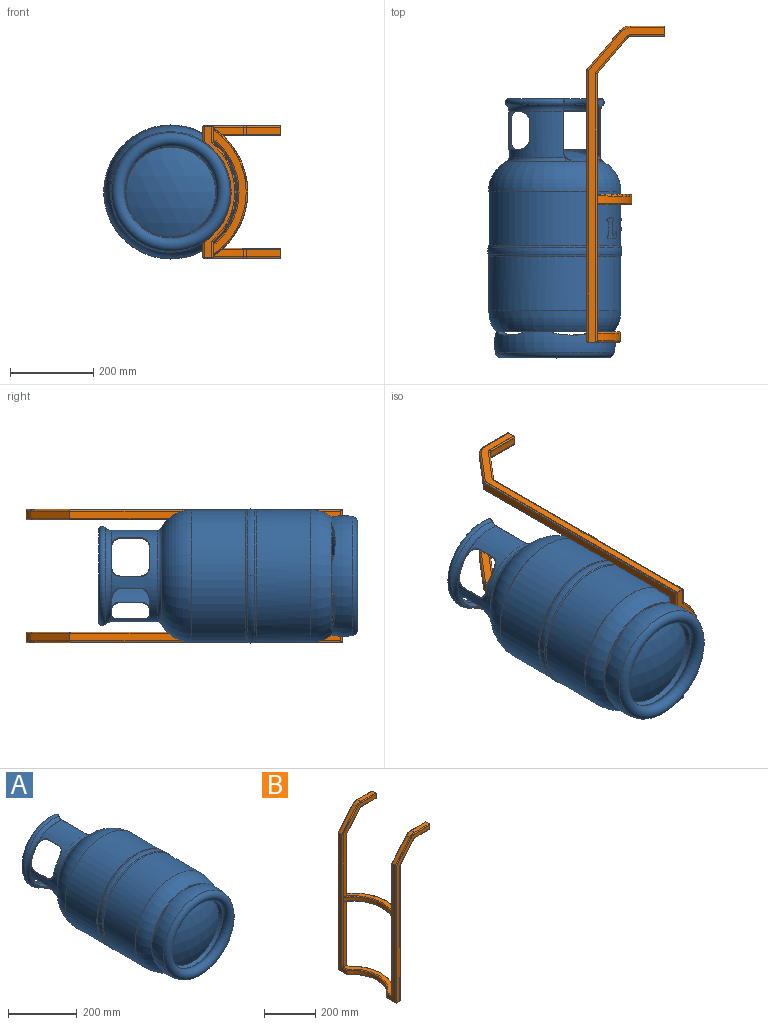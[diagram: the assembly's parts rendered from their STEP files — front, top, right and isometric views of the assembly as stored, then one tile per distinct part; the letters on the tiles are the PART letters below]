
ASSEMBLY  parts=2 mates=1
PART A: 195 faces, bbox 351.1x622.8x351.1 mm
  f0: torus R=127mm, axis (0,1,0), area 52168.6mm2, adj f16,f17
  f1: revolved ~322x161mm, area 9232mm2, adj f5,f6,f36
  f2: torus R=5mm, axis (0,-1,0), area 490.4mm2, adj f28,f32
  f3: torus R=110mm, axis (0,-1,0), area 22575.2mm2, adj f12,f13,f48,f52
  f4: cylinder r=159.1mm len=50mm, axis (0,-1,0), area 1436.8mm2, adj f128,f129,f130,f131,f132,f133,f134,f135
  f5: torus R=170mm, axis (0,-1,0), area 4380.5mm2, adj f1,f33,f36
  f6: torus R=170mm, axis (0,1,0), area 4380.5mm2, adj f1,f14,f36
  f7: torus R=121mm, axis (0,-1,0), area 6604.4mm2, adj f21,f32,f94,f95
  f8: cylinder r=1mm len=50mm, axis (0,-1,0), area 157.1mm2, adj f21,f22,f80,f81,f83,f86
  f9: cylinder r=1mm len=50mm, axis (0,-1,0), area 157.1mm2, adj f21,f22,f76,f77,f78,f79
  f10: cylinder r=1mm len=98.49mm, axis (0,-1,0), area 306.1mm2, adj f21,f22,f34,f53,f54,f55,f56
  f11: cylinder r=1mm len=98.49mm, axis (0,-1,0), area 306.1mm2, adj f21,f22,f35,f47,f49,f50,f51
  f12: torus R=130mm, axis (0,-1,0), area 8872.9mm2, adj f3,f21,f49,f54
  f13: torus R=88mm, axis (0,-1,0), area 7374.9mm2, adj f3,f22,f47,f53
  f14: cylinder r=159mm len=318mm, axis (0,-1,0), area 130299.4mm2, adj f6,f15
  f15: torus R=79mm, axis (0,-1,0), area 52435.7mm2, adj f14,f16,f38,f40,f42,f44,f46
  f16: torus R=46.35mm, axis (0,1,0), area 42883.7mm2, adj f0,f15,f37,f39,f41,f43,f45
  f17: torus R=46.35mm, axis (0,1,0), area 597.3mm2, adj f0,f18
  f18: torus R=79mm, axis (0,1,0), area 7285.3mm2, adj f17,f19
  f19: cone r=103.61mm half-angle=28.8deg, axis (0,-1,0), area 8167.4mm2, adj f18,f20
  f20: sphere r=244mm, area 39150.4mm2, adj f19
  f21: cylinder r=110mm len=220mm, axis (0,-1,0), area 31277mm2, adj f7,f8,f9,f10,f11,f12,f51,f56
  f22: cylinder r=108mm len=216mm, axis (0,-1,0), area 25755.8mm2, adj f8,f9,f10,f11,f13,f50,f55,f57
  f23: sphere r=242mm, area 38457.1mm2, adj f26
  f24: torus R=46.35mm, axis (0,1,0), area 8348mm2, adj f25,f31
  f25: torus R=79mm, axis (0,1,0), area 28085.8mm2, adj f24,f26,f37,f38,f39,f40,f41,f42
  f26: cone r=103.61mm half-angle=28.8deg, axis (0,-1,0), area 5650.5mm2, adj f23,f25
  f27: torus R=79mm, axis (0,-1,0), area 77657.1mm2, adj f32,f33
  f28: sphere r=242mm, area 45315.8mm2, adj f2,f29
  f29: torus R=79mm, axis (0,-1,0), area 74856.7mm2, adj f28,f30
  f30: cylinder r=157mm len=314mm, axis (0,-1,0), area 283545.1mm2, adj f29,f31
  f31: torus R=79mm, axis (0,-1,0), area 49322.8mm2, adj f24,f30
  f32: sphere r=244mm, area 32421.8mm2, adj f2,f7,f27,f91,f92,f93,f94,f95
  f33: cylinder r=159mm len=318mm, axis (0,-1,0), area 125889.8mm2, adj f5,f27,f96,f97,f98,f99,f100,f101
  f34: plane 29.04x15.75mm, normal (0.98,0,-0.19), area 234.1mm2, adj f10,f52,f53,f54
  f35: plane 29.04x16.04mm, normal (0,0,1), area 234.1mm2, adj f11,f47,f48,f49
  f36: revolved ~322x161mm, area 9232mm2, adj f1,f5,f6
  f37: bspline ~100x28.4mm, area 2391.9mm2, adj f16,f25,f38
  f38: plane 100x23.77mm, normal (0,-1,0), area 1389.2mm2, adj f15,f25,f37
  f39: bspline ~103.88x57.91mm, area 2394.9mm2, adj f16,f25,f40
  f40: plane 99.62x44.96mm, normal (0,-1,0), area 1389.2mm2, adj f15,f25,f39
  f41: bspline ~97.6x81.76mm, area 2394.9mm2, adj f16,f25,f42
  f42: plane 89.49x70.6mm, normal (0,-1,0), area 1389.2mm2, adj f15,f25,f41
  f43: bspline ~97.6x81.76mm, area 2394.9mm2, adj f16,f25,f44
  f44: plane 89.49x70.6mm, normal (0,-1,0), area 1389.2mm2, adj f15,f25,f43
  f45: bspline ~103.88x57.91mm, area 2394.9mm2, adj f16,f25,f46
  f46: plane 99.62x44.96mm, normal (0,-1,0), area 1389.2mm2, adj f15,f25,f45
  f47: bspline ~13.68x5.83mm, area 22.6mm2, adj f11,f13,f35,f48
  f48: bspline ~18.02x15.52mm, area 63.2mm2, adj f3,f35,f47,f49
  f49: bspline ~15.21x7.21mm, area 26mm2, adj f11,f12,f35,f48
  f50: bspline ~22.43x19.48mm, area 21.4mm2, adj f11,f22,f51,f91
  f51: bspline ~22.44x19.78mm, area 32mm2, adj f11,f21,f50,f94
  f52: bspline ~17.67x15.52mm, area 63.2mm2, adj f3,f34,f53,f54
  f53: bspline ~13.68x5.72mm, area 22.6mm2, adj f10,f13,f34,f52
  f54: bspline ~15.21x7.27mm, area 26mm2, adj f10,f12,f34,f52
  f55: bspline ~22.44x19.27mm, area 21.4mm2, adj f10,f22,f56,f93
  f56: bspline ~22.44x19.11mm, area 32mm2, adj f10,f21,f55,f95
  f57: bspline ~24.1x21mm, area 42.1mm2, adj f22,f58,f59,f60
  f58: cylinder r=1mm len=50mm, axis (0,-1,0), area 157.1mm2, adj f21,f22,f57,f59,f61,f64
  f59: bspline ~24.32x21.84mm, area 84.6mm2, adj f21,f57,f58,f60
  f60: torus R=109mm, axis (0,1,0), area 175.6mm2, adj f21,f22,f57,f59,f62,f65
  f61: bspline ~24.1x21mm, area 42.1mm2, adj f22,f58,f63,f64
  f62: bspline ~21x20.99mm, area 50.9mm2, adj f22,f60,f65,f66
  f63: torus R=109mm, axis (0,-1,0), area 175.6mm2, adj f21,f22,f61,f64,f67,f68
  f64: bspline ~24.32x21.84mm, area 84.6mm2, adj f21,f58,f61,f63
  f65: bspline ~21.19x21mm, area 49.9mm2, adj f21,f60,f62,f66
  f66: cylinder r=1mm len=50mm, axis (0,-1,0), area 157.1mm2, adj f21,f22,f62,f65,f67,f68
  f67: bspline ~21x20.99mm, area 50.9mm2, adj f22,f63,f66,f68
  f68: bspline ~21.19x21mm, area 49.9mm2, adj f21,f63,f66,f67
  f69: cylinder r=1mm len=50mm, axis (0,-1,0), area 157.1mm2, adj f21,f22,f70,f71,f72,f75
  f70: bspline ~21x19.7mm, area 50.9mm2, adj f22,f69,f72,f73
  f71: bspline ~21x19.7mm, area 50.9mm2, adj f22,f69,f74,f75
  f72: bspline ~21x19.58mm, area 49.9mm2, adj f21,f69,f70,f73
  f73: torus R=109mm, axis (0,-1,0), area 175.6mm2, adj f21,f22,f70,f72,f76,f78
  f74: torus R=109mm, axis (0,1,0), area 175.6mm2, adj f21,f22,f71,f75,f77,f79
  f75: bspline ~21x19.58mm, area 49.9mm2, adj f21,f69,f71,f74
  f76: bspline ~29.15x21mm, area 42.1mm2, adj f9,f22,f73,f78
  f77: bspline ~29.15x21mm, area 42.1mm2, adj f9,f22,f74,f79
  f78: bspline ~29.15x21mm, area 84.6mm2, adj f9,f21,f73,f76
  f79: bspline ~29.15x21mm, area 84.6mm2, adj f9,f21,f74,f77
  f80: bspline ~31.35x21mm, area 42.1mm2, adj f8,f22,f81,f82
  f81: bspline ~31.69x21mm, area 84.6mm2, adj f8,f21,f80,f82
  f82: torus R=109mm, axis (0,1,0), area 175.6mm2, adj f21,f22,f80,f81,f84,f87
  f83: bspline ~31.35x21mm, area 42.1mm2, adj f8,f22,f85,f86
  f84: bspline ~21x16.48mm, area 50.9mm2, adj f22,f82,f87,f88
  f85: torus R=109mm, axis (0,-1,0), area 175.6mm2, adj f21,f22,f83,f86,f89,f90
  f86: bspline ~31.69x21mm, area 84.6mm2, adj f8,f21,f83,f85
  f87: bspline ~21x16.05mm, area 49.9mm2, adj f21,f82,f84,f88
  f88: cylinder r=1mm len=50mm, axis (0,-1,0), area 157.1mm2, adj f21,f22,f84,f87,f89,f90
  f89: bspline ~21x16.48mm, area 50.9mm2, adj f22,f85,f88,f90
  f90: bspline ~21x16.05mm, area 49.9mm2, adj f21,f85,f88,f89
  f91: bspline ~20.46x17.75mm, area 230mm2, adj f32,f50,f92
  f92: torus R=97mm, axis (0,-1,0), area 10781.8mm2, adj f22,f32,f91,f93
  f93: bspline ~21.62x17.75mm, area 136.8mm2, adj f32,f55,f92
  f94: bspline ~14.32x9.77mm, area 60.1mm2, adj f7,f32,f51
  f95: bspline ~13.67x10.52mm, area 60.1mm2, adj f7,f32,f56
  f96: bspline ~2.35x1.08mm, area 0.3mm2, adj f33,f97,f126,f127
  f97: bspline ~2.75x1.31mm, area 0.3mm2, adj f33,f96,f98,f127
  f98: bspline ~1.42x0.73mm, area 0.2mm2, adj f33,f97,f99,f127
  f99: bspline ~3.44x2.37mm, area 0.5mm2, adj f33,f98,f100,f127
  f100: bspline ~8.32x2.63mm, area 0.9mm2, adj f33,f99,f101,f127
  f101: bspline ~6.88x4.97mm, area 1mm2, adj f33,f100,f102,f127
  f102: bspline ~3.65x1.77mm, area 0.4mm2, adj f33,f101,f103,f127
  f103: bspline ~3.28x2.69mm, area 0.4mm2, adj f33,f102,f104,f127
  f104: bspline ~8.24x4.71mm, area 1mm2, adj f33,f103,f105,f127
  f105: bspline ~12.23x9.41mm, area 1.8mm2, adj f33,f104,f106,f127
  f106: bspline ~14.19x4.13mm, area 1.5mm2, adj f33,f105,f107,f127
  f107: bspline ~7.92x4.67mm, area 1mm2, adj f33,f106,f108,f127
  f108: bspline ~4.53x3.93mm, area 0.7mm2, adj f33,f107,f109,f127
  f109: bspline ~2.5x0.95mm, area 0.3mm2, adj f33,f108,f110,f127
  f110: bspline ~2.6x1.11mm, area 0.3mm2, adj f33,f109,f111,f127
  f111: bspline ~3.37x3.34mm, area 0.5mm2, adj f33,f110,f112,f127
  f112: bspline ~4.1x3.67mm, area 0.6mm2, adj f33,f111,f113,f127
  f113: bspline ~9.09x3.95mm, area 1mm2, adj f33,f112,f114,f127
  f114: bspline ~8.99x4.58mm, area 1mm2, adj f33,f113,f115,f127
  f115: bspline ~4.29x3.41mm, area 0.6mm2, adj f33,f114,f116,f127
  f116: bspline ~3.27x2.84mm, area 0.5mm2, adj f33,f115,f117,f127
  f117: bspline ~2.41x2.15mm, area 0.4mm2, adj f33,f116,f118,f127
  f118: bspline ~9.58x5.38mm, area 1.1mm2, adj f33,f117,f119,f127
  f119: bspline ~15.22x6.45mm, area 1.8mm2, adj f33,f118,f120,f127
  f120: bspline ~13.69x4.32mm, area 1.5mm2, adj f33,f119,f121,f127
  f121: bspline ~10.14x9.95mm, area 1.5mm2, adj f33,f120,f122,f127
  f122: bspline ~11.73x2.89mm, area 1.2mm2, adj f33,f121,f123,f127
  f123: bspline ~12.11x3.42mm, area 1.3mm2, adj f33,f122,f124,f127
  f124: bspline ~10.05x9.51mm, area 1.4mm2, adj f33,f123,f125,f127
  f125: bspline ~12.6x3.99mm, area 1.4mm2, adj f33,f124,f126,f127
  f126: bspline ~8.18x3.25mm, area 0.9mm2, adj f33,f96,f125,f127
  f127: cylinder r=159.1mm len=51.88mm, axis (0,-1,0), area 1597mm2, adj f96,f97,f98,f99,f100,f101,f102,f103
  f128: bspline ~6.26x3.31mm, area 0.8mm2, adj f4,f33,f129,f150
  f129: bspline ~3.3x3.23mm, area 0.5mm2, adj f4,f33,f128,f130
  f130: bspline ~5.14x3.35mm, area 0.7mm2, adj f4,f33,f129,f131
  f131: bspline ~4.16x1.02mm, area 0.4mm2, adj f4,f33,f130,f132
  f132: plane 2.12x0.52mm, normal (0,1,0), area 0.2mm2, adj f4,f33,f131,f133
  f133: bspline ~14.05x2.18mm, area 1.4mm2, adj f4,f33,f132,f134
  f134: bspline ~3.76x0.44mm, area 0.4mm2, adj f4,f33,f133,f135
  f135: bspline ~10.4x2.38mm, area 1.1mm2, adj f4,f33,f134,f136
  f136: bspline ~13.04x7.95mm, area 1.6mm2, adj f4,f33,f135,f137
  f137: bspline ~11.59x5.41mm, area 1.3mm2, adj f4,f33,f136,f138
  f138: bspline ~12.32x4.08mm, area 1.3mm2, adj f4,f33,f137,f139
  f139: bspline ~4.5x0.5mm, area 0.5mm2, adj f4,f33,f138,f140
  f140: bspline ~1.76x0.29mm, area 0.2mm2, adj f4,f33,f139,f141
  f141: bspline ~1.18x1.01mm, area 0.2mm2, adj f4,f33,f140,f142
  f142: plane 0.22x0.1mm, normal (0.12,0,-0.99), area 0mm2, adj f4,f33,f141,f143
  f143: plane 5.97x0.22mm, normal (0.12,0.04,-0.99), area 0.6mm2, adj f4,f33,f142,f144
  f144: bspline ~4.37x2.51mm, area 0.5mm2, adj f4,f33,f143,f145
  f145: bspline ~2.77x2.01mm, area 0.4mm2, adj f4,f33,f144,f146
  f146: bspline ~12.71x4.76mm, area 1.5mm2, adj f4,f33,f145,f147
  f147: bspline ~12.6x4.57mm, area 1.5mm2, adj f4,f33,f146,f148
  f148: bspline ~3.3x2.99mm, area 0.5mm2, adj f4,f33,f147,f149
  f149: bspline ~9.79x1.66mm, area 1mm2, adj f4,f33,f148,f150
  f150: plane 18.93x0.1mm, normal (-0.22,0,0.98), area 1.9mm2, adj f4,f33,f128,f149
  f151: bspline ~1.58x0.61mm, area 0.2mm2, adj f4,f152,f158,f159
  f152: bspline ~2.59x0.48mm, area 0.3mm2, adj f4,f151,f153,f159
  f153: bspline ~3.94x1.25mm, area 0.4mm2, adj f4,f152,f154,f159
  f154: bspline ~6.02x2.31mm, area 0.7mm2, adj f4,f153,f155,f159
  f155: bspline ~6.36x2.7mm, area 0.7mm2, adj f4,f154,f156,f159
  f156: bspline ~4.12x1.25mm, area 0.4mm2, adj f4,f155,f157,f159
  f157: bspline ~2.62x1.32mm, area 0.3mm2, adj f4,f156,f158,f159
  f158: plane 11.49x0.1mm, normal (0.12,0,-0.99), area 1.1mm2, adj f4,f151,f157,f159
  f159: cylinder r=159mm len=14.87mm, axis (0,-1,0), area 114.7mm2, adj f151,f152,f153,f154,f155,f156,f157,f158
  f160: bspline ~7.05x0.85mm, area 0.7mm2, adj f33,f161,f185,f186
  f161: bspline ~4.2x2.33mm, area 0.5mm2, adj f33,f160,f162,f186
  f162: bspline ~8.35x7.19mm, area 1.3mm2, adj f33,f161,f163,f186
  f163: bspline ~2.27x2.27mm, area 0.4mm2, adj f33,f162,f164,f186
  f164: bspline ~6.07x4.03mm, area 0.8mm2, adj f33,f163,f165,f186
  f165: bspline ~9.41x3.07mm, area 1mm2, adj f33,f164,f166,f186
  f166: bspline ~3.43x2.77mm, area 0.5mm2, adj f33,f165,f167,f186
  f167: plane 7.15x3.51mm, normal (-0.04,-1,0.08), area 0.8mm2, adj f33,f166,f168,f186
  f168: plane 21.2x13.09mm, normal (0,-1,0), area 2.5mm2, adj f33,f167,f169,f186
  f169: bspline ~2.82x2.14mm, area 0.4mm2, adj f33,f168,f170,f186
  f170: bspline ~2.46x1.22mm, area 0.3mm2, adj f33,f169,f171,f186
  f171: bspline ~2.85x2.38mm, area 0.4mm2, adj f33,f170,f172,f186
  f172: bspline ~2.7x2.23mm, area 0.4mm2, adj f33,f171,f173,f186
  f173: bspline ~8.51x0.44mm, area 0.8mm2, adj f33,f172,f174,f186
  f174: bspline ~9.44x0.21mm, area 1mm2, adj f33,f173,f175,f186
  f175: bspline ~8.9x0.23mm, area 0.9mm2, adj f33,f174,f176,f186
  f176: bspline ~5.42x1.9mm, area 0.6mm2, adj f33,f175,f177,f186
  f177: bspline ~2.42x1.87mm, area 0.3mm2, adj f33,f176,f178,f186
  f178: bspline ~2.03x0.95mm, area 0.2mm2, adj f33,f177,f179,f186
  f179: bspline ~3.96x3.43mm, area 0.6mm2, adj f33,f178,f180,f186
  f180: bspline ~7.99x5.6mm, area 1mm2, adj f33,f179,f181,f186
  f181: bspline ~8.73x5.35mm, area 1mm2, adj f33,f180,f182,f186
  f182: bspline ~3.86x3.8mm, area 0.6mm2, adj f33,f181,f183,f186
  f183: bspline ~3.25x2.65mm, area 0.5mm2, adj f33,f182,f184,f186
  f184: bspline ~8.35x1.6mm, area 0.9mm2, adj f33,f183,f185,f186
  f185: plane 16.18x0.09mm, normal (0.49,0,-0.87), area 1.6mm2, adj f33,f160,f184,f186
  f186: cylinder r=159.1mm len=50mm, axis (0,-1,0), area 1167.1mm2, adj f160,f161,f162,f163,f164,f165,f166,f167
  f187: torus R=127mm, axis (0,1,0), area 21531.5mm2, adj f189,f194
  f188: torus R=79mm, axis (0,-1,0), area 15035.3mm2, adj f193,f194
  f189: torus R=127.77mm, axis (0,1,0), area 6349.9mm2, adj f187,f190
  f190: torus R=46.35mm, axis (0,1,0), area 12505.7mm2, adj f189,f191
  f191: torus R=127.88mm, axis (0,1,0), area 8510.9mm2, adj f190,f192
  f192: torus R=79mm, axis (0,1,0), area 5901mm2, adj f191,f193
  f193: cone r=117.54mm half-angle=28.8deg, axis (0,-1,0), area 1483.1mm2, adj f188,f192
  f194: torus R=46.35mm, axis (0,1,0), area 33508.6mm2, adj f187,f188
PART B: 210 faces, bbox 187.9x335.9x763.7 mm
  f0: plane 642.74x37.8mm, normal (-1,0,0), area 10836mm2, adj f1,f2,f9,f19,f162,f170,f175,f182
  f1: cylinder r=2.02mm len=309mm, axis (0,0,-1), area 965mm2, adj f0,f3,f175,f186
  f2: cylinder r=2.02mm len=291.43mm, axis (0,0,-1), area 912mm2, adj f0,f3,f20,f185
  f3: plane 733.02x182.8mm, normal (0,-1,0), area 13983.8mm2, adj f1,f2,f10,f20,f21,f32,f33,f44
  f4: plane 731.97x183.75mm, normal (0,1,0), area 14021.9mm2, adj f5,f6,f17,f24,f29,f36,f41,f48
  f5: cylinder r=4mm len=309mm, axis (0,0,-1), area 1928.9mm2, adj f4,f7,f74,f166
  f6: cylinder r=4mm len=291.43mm, axis (0,0,-1), area 1826.5mm2, adj f4,f7,f24,f78
  f7: plane 642.03x36.86mm, normal (1,0,0), area 10839.6mm2, adj f5,f6,f13,f25,f74,f78,f79,f80
  f8: plane 753.4x182.18mm, normal (0,1,0), area 14694mm2, adj f9,f12,f18,f23,f30,f35,f42,f47
  f9: cylinder r=2.02mm len=644.43mm, axis (0,0,-1), area 2014.9mm2, adj f0,f8,f18,f170
  f10: cylinder r=2.02mm len=632.42mm, axis (0,0,-1), area 1977.2mm2, adj f3,f11,f21,f173
  f11: plane 649.42x46.98mm, normal (1,0,0), area 11549.8mm2, adj f10,f12,f22,f172,f173,f176
  f12: cylinder r=2.02mm len=651.42mm, axis (0,0,-1), area 2036.8mm2, adj f8,f11,f23,f172
  f13: cylinder r=4mm len=646.43mm, axis (0,0,-1), area 4044.4mm2, adj f7,f14,f26,f165
  f14: plane 755.23x182mm, normal (0,-1,0), area 14736mm2, adj f13,f15,f26,f27,f38,f39,f48,f51
  f15: cylinder r=4mm len=654.15mm, axis (0,0,-1), area 4092.9mm2, adj f14,f16,f27,f163
  f16: plane 650.15x47.96mm, normal (-1,0,0), area 11578.9mm2, adj f15,f17,f28,f154,f163,f168
  f17: cylinder r=4mm len=633.15mm, axis (0,0,-1), area 3961mm2, adj f4,f16,f29,f168
  f18: cylinder r=2.02mm len=89.04mm, axis (-0.65,0,-0.76), area 359.6mm2, adj f8,f9,f19,f30
  f19: plane 87.18x74.1mm, normal (-0.76,0,0.65), area 1945.1mm2, adj f0,f18,f20,f31
  f20: cylinder r=2.02mm len=89.04mm, axis (-0.65,0,-0.76), area 359.6mm2, adj f2,f3,f19,f32
  f21: cylinder r=2.02mm len=94.36mm, axis (-0.65,0,-0.76), area 381.5mm2, adj f3,f10,f22,f33
  f22: plane 93.06x79.1mm, normal (0.76,0,-0.65), area 2076.3mm2, adj f11,f21,f23,f34
  f23: cylinder r=2.02mm len=94.36mm, axis (-0.65,0,-0.76), area 381.5mm2, adj f8,f12,f22,f35
  f24: cylinder r=4mm len=90.33mm, axis (-0.65,0,-0.76), area 718.9mm2, adj f4,f6,f25,f36
  f25: plane 86.62x73.62mm, normal (0.76,0,-0.65), area 1932.6mm2, adj f7,f24,f26,f37
  f26: cylinder r=4mm len=90.33mm, axis (-0.65,0,-0.76), area 718.9mm2, adj f13,f14,f25,f38
  f27: cylinder r=4mm len=96.21mm, axis (-0.65,0,-0.76), area 767.4mm2, adj f14,f15,f28,f39
  f28: plane 93.62x79.58mm, normal (-0.76,0,0.65), area 2088.8mm2, adj f16,f27,f29,f40
  f29: cylinder r=4mm len=96.21mm, axis (-0.65,0,-0.76), area 767.4mm2, adj f4,f17,f28,f41
  f30: torus R=11.52mm, axis (0,-1,0), area 27.8mm2, adj f8,f18,f31,f42
  f31: cylinder r=9.5mm len=17mm, axis (0,-1,0), area 139.9mm2, adj f19,f30,f32,f43
  f32: torus R=11.52mm, axis (0,-1,0), area 27.8mm2, adj f3,f20,f31,f44
  f33: torus R=28.48mm, axis (0,-1,0), area 80.8mm2, adj f3,f21,f34,f45
  f34: cylinder r=30.5mm len=23.24mm, axis (0,-1,0), area 449.2mm2, adj f22,f33,f35,f46
  f35: torus R=28.48mm, axis (0,-1,0), area 80.8mm2, adj f8,f23,f34,f47
  f36: torus R=11.5mm, axis (0,-1,0), area 48.7mm2, adj f4,f24,f37,f49
  f37: cylinder r=7.5mm len=17mm, axis (0,-1,0), area 110.5mm2, adj f25,f36,f38,f50
  f38: torus R=11.5mm, axis (0,-1,0), area 48.7mm2, adj f14,f26,f37,f51
  f39: torus R=28.5mm, axis (0,-1,0), area 169mm2, adj f14,f27,f40,f52
  f40: cylinder r=32.5mm len=24.76mm, axis (0,-1,0), area 478.6mm2, adj f28,f39,f41,f53
  f41: torus R=28.5mm, axis (0,-1,0), area 169mm2, adj f4,f29,f40,f54
  f42: cylinder r=2.02mm len=81.66mm, axis (-1,0,0), area 255.9mm2, adj f8,f30,f43,f48
  f43: plane 81.66x17mm, normal (0,0,1), area 1388.3mm2, adj f31,f42,f44,f48
  f44: cylinder r=2.02mm len=81.66mm, axis (-1,0,0), area 255.9mm2, adj f3,f32,f43,f48
  f45: cylinder r=2.02mm len=81.66mm, axis (-1,0,0), area 255.9mm2, adj f3,f33,f46,f48
  f46: plane 81.66x17mm, normal (0,0,-1), area 1388.3mm2, adj f34,f45,f47,f48
  f47: cylinder r=2.02mm len=81.66mm, axis (-1,0,0), area 255.9mm2, adj f8,f35,f46,f48
  f48: plane 25x25mm, normal (1,0,0), area 173.8mm2, adj f3,f4,f8,f14,f42,f43,f44,f45
  f49: cylinder r=4mm len=81.66mm, axis (-1,0,0), area 513.1mm2, adj f4,f36,f48,f50
  f50: plane 81.66x17mm, normal (0,0,-1), area 1388.3mm2, adj f37,f48,f49,f51
  f51: cylinder r=4mm len=81.66mm, axis (-1,0,0), area 513.1mm2, adj f14,f38,f48,f50
  f52: cylinder r=4mm len=81.66mm, axis (-1,0,0), area 513.1mm2, adj f14,f39,f48,f53
  f53: plane 81.66x17mm, normal (0,0,1), area 1388.3mm2, adj f40,f48,f52,f54
  f54: cylinder r=4mm len=81.66mm, axis (-1,0,0), area 513.1mm2, adj f4,f41,f48,f53
  f55: plane 21.9x12.38mm, normal (0,1,0), area 237.9mm2, adj f57,f67,f68,f71,f72,f73
  f56: plane 21.51x14.81mm, normal (-1,0,0), area 298.2mm2, adj f57,f64,f65,f66,f67,f68
  f57: cylinder r=2.02mm len=21mm, axis (0,0,1), area 65.8mm2, adj f55,f56,f67,f68
  f58: plane 25x21mm, normal (-0.86,0.52,0), area 165.5mm2, adj f59,f61,f62,f63,f64,f65,f66,f67
  f59: torus R=181mm, axis (0,0,1), area 37.5mm2, adj f58,f60,f63,f132,f142
  f60: cylinder r=185mm len=17mm, axis (0,0,1), area 74.4mm2, adj f59,f61,f132,f142
  f61: torus R=181mm, axis (0,0,1), area 37.5mm2, adj f58,f60,f62,f132,f142
  f62: plane 17.77x14.91mm, normal (0,0,1), area 180mm2, adj f58,f61,f69,f125,f129,f142
  f63: plane 17.77x14.91mm, normal (0,0,-1), area 180mm2, adj f58,f59,f70,f129,f131,f142
  f64: torus R=180.98mm, axis (0,0,1), area 20.7mm2, adj f56,f58,f65,f68
  f65: cylinder r=183mm len=17mm, axis (0,0,1), area 101.5mm2, adj f56,f58,f64,f66
  f66: torus R=180.98mm, axis (0,0,1), area 20.7mm2, adj f56,f58,f65,f67
  f67: plane 17.77x14.91mm, normal (0,0,1), area 180mm2, adj f55,f56,f57,f58,f66,f71
  f68: plane 17.77x14.91mm, normal (0,0,-1), area 180mm2, adj f55,f56,f57,f58,f64,f73
  f69: torus R=164mm, axis (0,0,1), area 14.8mm2, adj f58,f62,f129
  f70: torus R=164mm, axis (0,0,1), area 14.8mm2, adj f58,f63,f129
  f71: torus R=164.02mm, axis (0,0,1), area 14mm2, adj f55,f58,f67,f72
  f72: cylinder r=162mm len=17mm, axis (0,0,1), area 49.2mm2, adj f55,f58,f71,f73
  f73: torus R=164.02mm, axis (0,0,1), area 14mm2, adj f55,f58,f68,f72
  f74: plane 299.12x87.88mm, normal (0,0,-1), area 5566.7mm2, adj f4,f5,f7,f75,f81,f121,f130,f138
  f75: torus R=164mm, axis (0,0,1), area 1999.5mm2, adj f4,f74,f76,f121
  f76: cylinder r=160mm len=270mm, axis (0,0,1), area 5463mm2, adj f4,f75,f77,f121
  f77: torus R=164mm, axis (0,0,1), area 1999.5mm2, adj f4,f76,f78,f121
  f78: plane 299.12x87.88mm, normal (0,0,1), area 5566.7mm2, adj f4,f6,f7,f77,f79,f120,f121,f138
  f79: torus R=181mm, axis (0,0,1), area 2260.1mm2, adj f7,f78,f80,f138
  f80: cylinder r=185mm len=308.76mm, axis (0,0,1), area 6209.4mm2, adj f7,f79,f81,f138
  f81: torus R=181mm, axis (0,0,1), area 2260.1mm2, adj f7,f74,f80,f138
  f82: cylinder r=4mm len=81.66mm, axis (1,0,0), area 513.1mm2, adj f83,f88,f95,f124
  f83: plane 81.66x17mm, normal (0,0,-1), area 1388.3mm2, adj f82,f84,f88,f96
  f84: cylinder r=4mm len=81.66mm, axis (1,0,0), area 513.1mm2, adj f83,f88,f97,f121
  f85: cylinder r=4mm len=81.66mm, axis (1,0,0), area 513.1mm2, adj f86,f88,f98,f121
  f86: plane 81.66x17mm, normal (0,0,1), area 1388.3mm2, adj f85,f87,f88,f99
  f87: cylinder r=4mm len=81.66mm, axis (1,0,0), area 513.1mm2, adj f86,f88,f100,f124
  f88: plane 25x25mm, normal (1,0,0), area 173.8mm2, adj f82,f83,f84,f85,f86,f87,f89,f90
  f89: cylinder r=2.02mm len=81.66mm, axis (1,0,0), area 255.9mm2, adj f88,f90,f101,f129
  f90: plane 81.66x17mm, normal (0,0,1), area 1388.3mm2, adj f88,f89,f91,f102
  f91: cylinder r=2.02mm len=81.66mm, axis (1,0,0), area 255.9mm2, adj f88,f90,f103,f132
  f92: cylinder r=2.02mm len=81.66mm, axis (1,0,0), area 255.9mm2, adj f88,f93,f104,f132
  f93: plane 81.66x17mm, normal (0,0,-1), area 1388.3mm2, adj f88,f92,f94,f105
  f94: cylinder r=2.02mm len=81.66mm, axis (1,0,0), area 255.9mm2, adj f88,f93,f106,f129
  f95: torus R=11.5mm, axis (0,1,0), area 48.7mm2, adj f82,f96,f107,f124
  f96: cylinder r=7.5mm len=17mm, axis (0,1,0), area 110.5mm2, adj f83,f95,f97,f108
  f97: torus R=11.5mm, axis (0,1,0), area 48.7mm2, adj f84,f96,f109,f121
  f98: torus R=28.5mm, axis (0,1,0), area 169mm2, adj f85,f99,f110,f121
  f99: cylinder r=32.5mm len=24.76mm, axis (0,1,0), area 478.6mm2, adj f86,f98,f100,f111
  f100: torus R=28.5mm, axis (0,1,0), area 169mm2, adj f87,f99,f112,f124
  f101: torus R=11.52mm, axis (0,1,0), area 27.8mm2, adj f89,f102,f113,f129
  f102: cylinder r=9.5mm len=17mm, axis (0,1,0), area 139.9mm2, adj f90,f101,f103,f114
  f103: torus R=11.52mm, axis (0,1,0), area 27.8mm2, adj f91,f102,f115,f132
  f104: torus R=28.48mm, axis (0,1,0), area 80.8mm2, adj f92,f105,f116,f132
  f105: cylinder r=30.5mm len=23.24mm, axis (0,1,0), area 449.2mm2, adj f93,f104,f106,f117
  f106: torus R=28.48mm, axis (0,1,0), area 80.8mm2, adj f94,f105,f118,f129
  f107: cylinder r=4mm len=90.33mm, axis (0.65,0,0.76), area 718.9mm2, adj f95,f108,f119,f124
  f108: plane 86.62x73.62mm, normal (0.76,0,-0.65), area 1932.6mm2, adj f96,f107,f109,f138
  f109: cylinder r=4mm len=90.33mm, axis (0.65,0,0.76), area 718.9mm2, adj f97,f108,f120,f121
  f110: cylinder r=4mm len=96.21mm, axis (0.65,0,0.76), area 767.4mm2, adj f98,f111,f121,f122
  f111: plane 93.62x79.58mm, normal (-0.76,0,0.65), area 2088.8mm2, adj f99,f110,f112,f135
  f112: cylinder r=4mm len=96.21mm, axis (0.65,0,0.76), area 767.4mm2, adj f100,f111,f123,f124
  f113: cylinder r=2.02mm len=89.04mm, axis (0.65,0,0.76), area 359.6mm2, adj f101,f114,f125,f129
  f114: plane 87.18x74.1mm, normal (-0.76,0,0.65), area 1945.1mm2, adj f102,f113,f115,f142
  f115: cylinder r=2.02mm len=89.04mm, axis (0.65,0,0.76), area 359.6mm2, adj f103,f114,f126,f132
  f116: cylinder r=2.02mm len=94.36mm, axis (0.65,0,0.76), area 381.5mm2, adj f104,f117,f127,f132
  f117: plane 93.06x79.1mm, normal (0.76,0,-0.65), area 2076.3mm2, adj f105,f116,f118,f145
  f118: cylinder r=2.02mm len=94.36mm, axis (0.65,0,0.76), area 381.5mm2, adj f106,f117,f128,f129
  f119: cylinder r=4mm len=646.43mm, axis (0,0,1), area 4044.4mm2, adj f107,f124,f137,f138
  f120: cylinder r=4mm len=291.43mm, axis (0,0,1), area 1826.5mm2, adj f78,f109,f121,f138
  f121: plane 731.97x183.75mm, normal (0,-1,0), area 14021.9mm2, adj f74,f75,f76,f77,f78,f84,f85,f88
  f122: cylinder r=4mm len=633.15mm, axis (0,0,1), area 3961mm2, adj f110,f121,f134,f135
  f123: cylinder r=4mm len=654.15mm, axis (0,0,1), area 4092.9mm2, adj f112,f124,f135,f136
  f124: plane 755.23x182mm, normal (0,1,0), area 14736mm2, adj f82,f87,f88,f95,f100,f107,f112,f119
  f125: cylinder r=2.02mm len=291.43mm, axis (0,0,1), area 912mm2, adj f62,f113,f129,f142
  f126: cylinder r=2.02mm len=644.43mm, axis (0,0,1), area 2014.9mm2, adj f115,f132,f142,f143
  f127: cylinder r=2.02mm len=651.42mm, axis (0,0,1), area 2036.8mm2, adj f116,f132,f144,f145
  f128: cylinder r=2.02mm len=632.42mm, axis (0,0,1), area 1977.2mm2, adj f118,f129,f140,f145
  f129: plane 733.02x182.8mm, normal (0,1,0), area 13983.8mm2, adj f58,f62,f63,f69,f70,f88,f89,f94
  f130: cylinder r=4mm len=309mm, axis (0,0,1), area 1928.9mm2, adj f74,f121,f133,f138
  f131: cylinder r=2.02mm len=309mm, axis (0,0,1), area 965mm2, adj f63,f129,f141,f142
  f132: plane 753.4x182.18mm, normal (0,-1,0), area 14694mm2, adj f58,f59,f60,f61,f88,f91,f92,f103
  f133: cylinder r=4mm len=20.74mm, axis (0,1,0), area 111.6mm2, adj f130,f138,f139,f167
  f134: cylinder r=4mm len=30.96mm, axis (0,1,0), area 174.1mm2, adj f122,f135,f153,f167
  f135: plane 650.15x47.96mm, normal (-1,0,0), area 11578.9mm2, adj f111,f122,f123,f134,f136,f153
  f136: cylinder r=4mm len=51.96mm, axis (0,1,0), area 312.9mm2, adj f123,f135,f153,f164
  f137: cylinder r=4mm len=41.74mm, axis (0,1,0), area 243.5mm2, adj f119,f138,f139,f164
  f138: plane 642.03x36.86mm, normal (1,0,0), area 10839.5mm2, adj f74,f78,f79,f80,f81,f108,f119,f120
  f139: plane 25.82x4.82mm, normal (0.44,-0.9,0), area 3.1mm2, adj f133,f137,f138,f148,f149,f150
  f140: cylinder r=2.02mm len=29.98mm, axis (0,1,0), area 89.3mm2, adj f128,f145,f146,f174
  f141: cylinder r=2.02mm len=20.74mm, axis (0,1,0), area 60.3mm2, adj f131,f142,f161,f174
  f142: plane 642.74x37.8mm, normal (-1,0,0), area 10836mm2, adj f59,f60,f61,f62,f63,f114,f125,f126
  f143: cylinder r=2.02mm len=39.74mm, axis (0,1,0), area 119.8mm2, adj f126,f142,f161,f171
  f144: cylinder r=2.02mm len=48.98mm, axis (0,1,0), area 148.8mm2, adj f127,f145,f146,f171
  f145: plane 649.42x46.98mm, normal (1,0,0), area 11549.8mm2, adj f117,f127,f128,f140,f144,f146
  f146: plane 21.41x2.51mm, normal (0.44,-0.9,0), area 2.3mm2, adj f140,f144,f145,f156,f157,f158,f171,f174
  f147: torus R=136.5mm, axis (0,0,1), area 1589.9mm2, adj f152,f153,f154,f164
  f148: torus R=153.5mm, axis (0,0,1), area 1709.7mm2, adj f139,f149,f164,f169
  f149: cylinder r=157.5mm len=240.31mm, axis (0,0,1), area 4647mm2, adj f139,f148,f150,f169
  f150: torus R=153.5mm, axis (0,0,1), area 1709.7mm2, adj f139,f149,f167,f169
  f151: torus R=136.5mm, axis (0,0,1), area 1589.9mm2, adj f152,f153,f154,f167
  f152: cylinder r=132.5mm len=215.95mm, axis (0,0,1), area 4291.2mm2, adj f147,f151,f153,f154
  f153: plane 25.82x4.9mm, normal (-0.44,0.9,0), area 3.8mm2, adj f134,f135,f136,f147,f151,f152
  f154: plane 25.82x4.9mm, normal (-0.44,-0.9,0), area 3.8mm2, adj f16,f147,f151,f152,f163,f168
  f155: torus R=153.48mm, axis (0,0,1), area 849.2mm2, adj f160,f161,f162,f171
  f156: torus R=136.52mm, axis (0,0,1), area 797mm2, adj f146,f157,f171,f176
  f157: cylinder r=134.5mm len=217.94mm, axis (0,0,1), area 4318.9mm2, adj f146,f156,f158,f176
  f158: torus R=136.52mm, axis (0,0,1), area 797mm2, adj f146,f157,f174,f176
  f159: torus R=153.48mm, axis (0,0,1), area 849.2mm2, adj f160,f161,f162,f174
  f160: cylinder r=155.5mm len=238.4mm, axis (0,0,1), area 4617.9mm2, adj f155,f159,f161,f162
  f161: plane 21.4x2.42mm, normal (-0.44,0.9,0), area 1.9mm2, adj f141,f142,f143,f155,f159,f160
  f162: plane 21.4x2.4mm, normal (-0.44,-0.9,0), area 1.9mm2, adj f0,f155,f159,f160,f170,f175
  f163: cylinder r=4mm len=51.96mm, axis (0,1,0), area 312.9mm2, adj f15,f16,f154,f164
  f164: plane 320x72.62mm, normal (0,0,-1), area 6026.9mm2, adj f14,f124,f136,f137,f147,f148,f163,f165
  f165: cylinder r=4mm len=41.74mm, axis (0,1,0), area 243.5mm2, adj f7,f13,f164,f169
  f166: cylinder r=4mm len=20.74mm, axis (0,1,0), area 111.6mm2, adj f5,f7,f167,f169
  f167: plane 270x72.62mm, normal (0,0,1), area 5176.9mm2, adj f4,f121,f133,f134,f150,f151,f166,f168
  f168: cylinder r=4mm len=30.96mm, axis (0,1,0), area 174.1mm2, adj f16,f17,f154,f167
  f169: plane 25.82x4.82mm, normal (0.44,0.9,0), area 3.1mm2, adj f7,f148,f149,f150,f165,f166
  f170: cylinder r=2.02mm len=39.74mm, axis (0,1,0), area 119.8mm2, adj f0,f9,f162,f171
  f171: plane 316x72.62mm, normal (0,0,1), area 5958.9mm2, adj f8,f132,f143,f144,f146,f155,f156,f170
  f172: cylinder r=2.02mm len=48.98mm, axis (0,1,0), area 148.8mm2, adj f11,f12,f171,f176
  f173: cylinder r=2.02mm len=29.98mm, axis (0,1,0), area 89.3mm2, adj f10,f11,f174,f176
  f174: plane 274x72.62mm, normal (0,0,-1), area 5244.9mm2, adj f3,f129,f140,f141,f146,f158,f159,f173
  f175: cylinder r=2.02mm len=20.74mm, axis (0,1,0), area 60.3mm2, adj f0,f1,f162,f174
  f176: plane 21.41x2.51mm, normal (0.44,0.9,0), area 2.3mm2, adj f11,f156,f157,f158,f171,f172,f173,f174
  f177: torus R=164mm, axis (0,0,1), area 14.8mm2, adj f3,f185,f192
  f178: torus R=164mm, axis (0,0,1), area 14.8mm2, adj f3,f186,f192
  f179: torus R=164.02mm, axis (0,0,1), area 14mm2, adj f180,f190,f192,f193
  f180: cylinder r=162mm len=17mm, axis (0,0,1), area 49.2mm2, adj f179,f181,f192,f193
  f181: torus R=164.02mm, axis (0,0,1), area 14mm2, adj f180,f191,f192,f193
  f182: torus R=181mm, axis (0,0,1), area 37.5mm2, adj f0,f8,f183,f186,f192
  f183: cylinder r=185mm len=17mm, axis (0,0,1), area 74.4mm2, adj f0,f8,f182,f184
  f184: torus R=181mm, axis (0,0,1), area 37.5mm2, adj f0,f8,f183,f185,f192
  f185: plane 17.77x14.91mm, normal (0,0,1), area 180mm2, adj f0,f2,f3,f177,f184,f192
  f186: plane 17.77x14.91mm, normal (0,0,-1), area 180mm2, adj f0,f1,f3,f178,f182,f192
  f187: torus R=180.98mm, axis (0,0,1), area 20.7mm2, adj f188,f191,f192,f195
  f188: cylinder r=183mm len=17mm, axis (0,0,1), area 101.5mm2, adj f187,f189,f192,f195
  f189: torus R=180.98mm, axis (0,0,1), area 20.7mm2, adj f188,f190,f192,f195
  f190: plane 17.77x14.91mm, normal (0,0,1), area 180mm2, adj f179,f189,f192,f193,f194,f195
  f191: plane 17.77x14.91mm, normal (0,0,-1), area 180mm2, adj f181,f187,f192,f193,f194,f195
  f192: plane 25x21mm, normal (-0.86,-0.52,0), area 165.5mm2, adj f3,f8,f177,f178,f179,f180,f181,f182
  f193: plane 21.9x12.38mm, normal (0,-1,0), area 237.9mm2, adj f179,f180,f181,f190,f191,f194
  f194: cylinder r=2.02mm len=21mm, axis (0,0,-1), area 65.8mm2, adj f190,f191,f193,f195
  f195: plane 21.51x14.81mm, normal (-1,0,0), area 298.2mm2, adj f187,f188,f189,f190,f191,f194
  f196: plane 21.53x13.5mm, normal (1,0,0), area 270.4mm2, adj f197,f199,f200,f201,f202,f203
  f197: cylinder r=4mm len=21mm, axis (0,0,1), area 131.9mm2, adj f196,f198,f199,f200
  f198: plane 21.88x9.27mm, normal (0,-1,0), area 173.1mm2, adj f197,f199,f200,f204,f205,f206
  f199: plane 299.12x87.88mm, normal (0,0,-1), area 5566.7mm2, adj f196,f197,f198,f203,f204,f207,f208,f209
  f200: plane 299.12x87.88mm, normal (0,0,1), area 5566.7mm2, adj f196,f197,f198,f201,f206,f207,f208,f209
  f201: torus R=180.98mm, axis (0,0,1), area 1115.1mm2, adj f196,f200,f202,f207
  f202: cylinder r=183mm len=303.95mm, axis (0,0,1), area 6097.2mm2, adj f196,f201,f203,f207
  f203: torus R=180.98mm, axis (0,0,1), area 1115.1mm2, adj f196,f199,f202,f207
  f204: torus R=164.02mm, axis (0,0,1), area 995.3mm2, adj f198,f199,f205,f209
  f205: cylinder r=162mm len=270mm, axis (0,0,1), area 5426mm2, adj f198,f204,f206,f209
  f206: torus R=164.02mm, axis (0,0,1), area 995.3mm2, adj f198,f200,f205,f209
  f207: plane 21.53x13.5mm, normal (1,0,0), area 270.4mm2, adj f199,f200,f201,f202,f203,f208
  f208: cylinder r=4mm len=21mm, axis (0,0,-1), area 131.9mm2, adj f199,f200,f207,f209
  f209: plane 21.88x9.27mm, normal (0,1,0), area 173.1mm2, adj f199,f200,f204,f205,f206,f208
PLACE A t=(-197.87,-90.11,118.17)mm
PLACE B rot(axis=(-1,0,0),90deg) t=(-108.43,-296.76,-29.33)mm
MATE revolute B.f59 <-> A.f15  axis (0,1,0) through (-197.87,-284.26,118.17)mm
